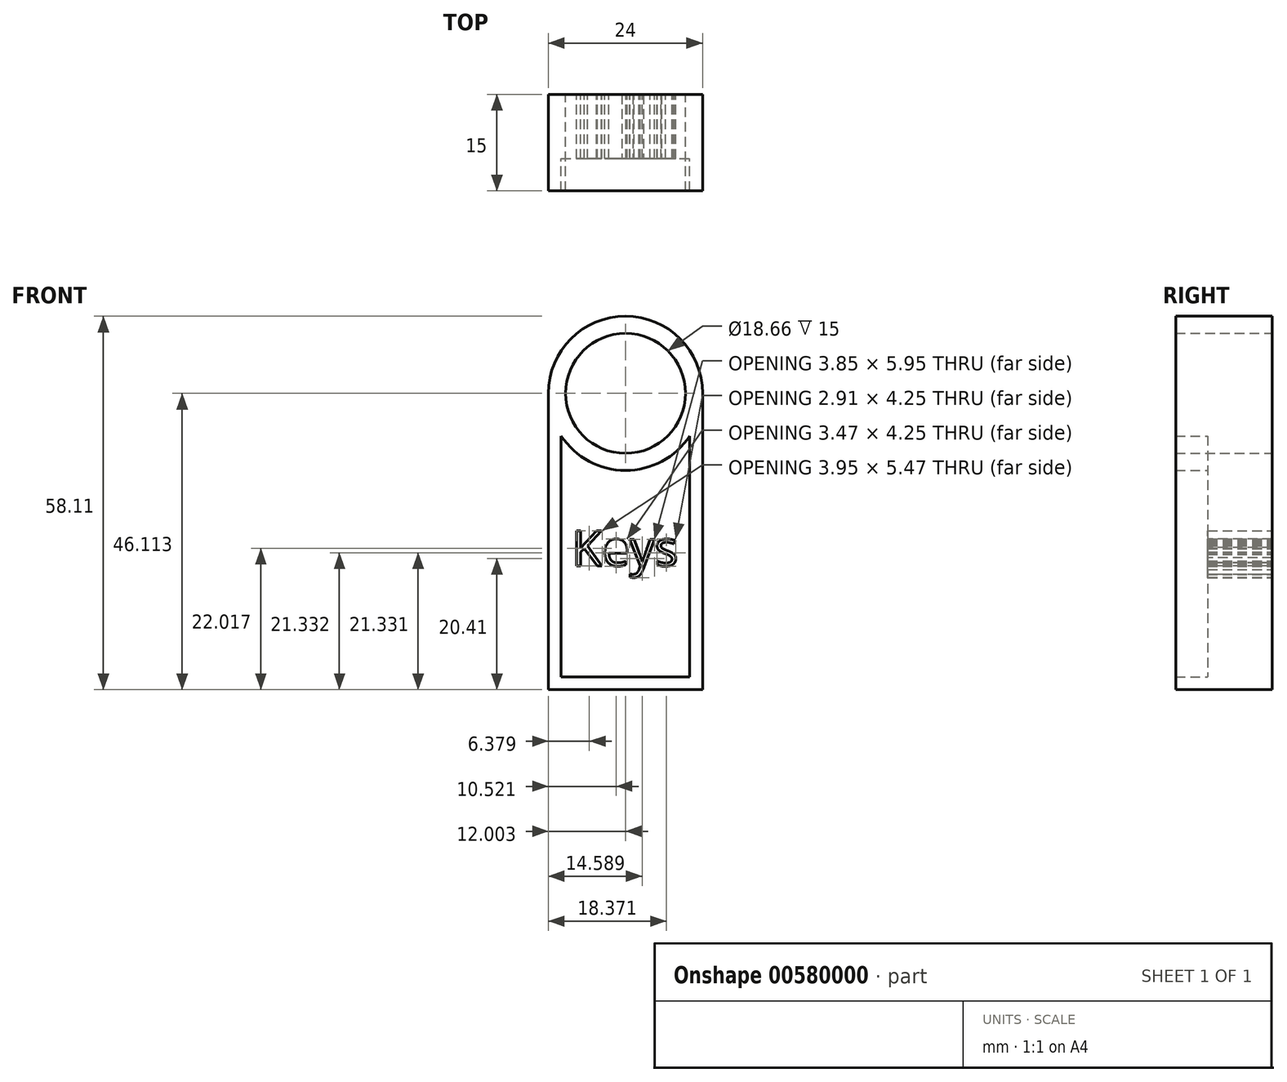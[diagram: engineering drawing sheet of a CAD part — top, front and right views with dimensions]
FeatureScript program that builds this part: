
annotation { "Feature Type Name" : "Feature", "Feature Type Description" : "" }
export const myFeature = defineFeature(function(context is Context, id is Id, definition is map)
    precondition{}
    {
        {
            var Q0;
            Q0=qCreatedBy(makeId("Front.planeOp"),FACE);
            var sketch = newSketch(context, id + "F0", { "sketchPlane" : qUnion([Q0])});
            skCircle(sketch, "E0", {"center": v(-22.42, 46.11) * mm, "radius": 12 * mm});
            skCircle(sketch, "E1", {"center": v(-22.42, 46.11) * mm, "radius": 9.33 * mm});
            skLineSegment(sketch, "E2", {"start": v(-34.42, 46.11) * mm, "end": v(-34.42, 0) * mm});
            skLineSegment(sketch, "E3", {"start": v(-34.42, 0) * mm, "end": v(-10.42, 0) * mm});
            skLineSegment(sketch, "E4", {"start": v(-10.42, 0) * mm, "end": v(-10.42, 46.11) * mm});
            skLineSegment(sketch, "E5", {"start": v(-32.42, 39.48) * mm, "end": v(-32.42, 2) * mm});
            skLineSegment(sketch, "E6", {"start": v(-32.42, 2) * mm, "end": v(-12.42, 2) * mm});
            skLineSegment(sketch, "E7", {"start": v(-12.42, 2) * mm, "end": v(-12.42, 39.48) * mm});
            skText(sketch, "E8", { "text": "Keys", "fontName": "OpenSans-Regular.ttf"});
            const initialGuessF0  = {"E8": [-0.03077, 0.01928, 1, 0, 0.00552]};
            skSetInitialGuess(sketch, initialGuessF0);
            skSolve(sketch);
        }
        {
            var Q0;
            Q0 = qSketchRegion(id + "F0", true);
            extrude(context, id + "F1", {"entities" : qUnion([Q0]), "depth" : 15 * mm, "offsetDistance" : 25 * mm});
        }
        {
            var Q0;
            {var subQ0=sQuery(id+"F0.wireOp",EDGE,"E5");Q0=makeQuery(id+"F0.imprint","IMPRINT",FACE,{"disambiguationData":[TD([[makeQuery(id+"F0.imprint","IMPRINT",EDGE,{"derivedFrom":subQ0}),1.0]])]});}
            extrude(context, id + "F2", {"entities" : qUnion([Q0]), "operationType" : NewBodyOperationType.ADD, "depth" : 10 * mm, "offsetDistance" : 25 * mm});
        }
    });
